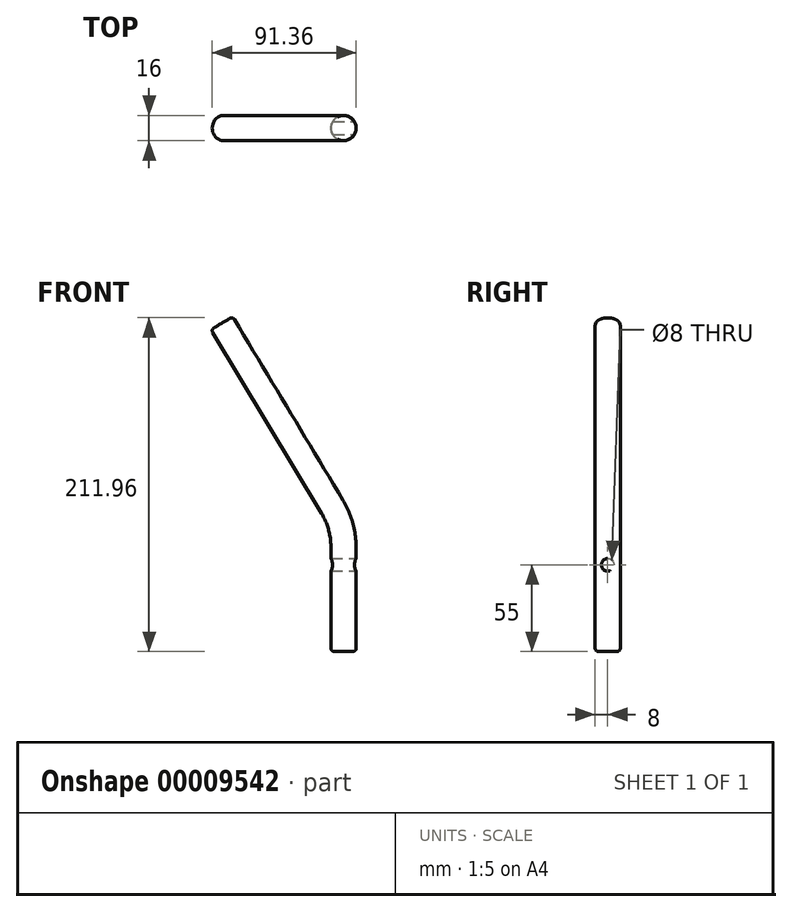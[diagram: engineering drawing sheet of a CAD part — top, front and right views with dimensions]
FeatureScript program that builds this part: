
annotation { "Feature Type Name" : "Feature", "Feature Type Description" : "" }
export const myFeature = defineFeature(function(context is Context, id is Id, definition is map)
    precondition{}
    {
        {
            var Q0;
            Q0=qCreatedBy(makeId("Top.planeOp"),FACE);
            var sketch = newSketch(context, id + "F0", { "sketchPlane" : qUnion([Q0])});
            skCircle(sketch, "E0", {"center": v(0, 0) * mm, "radius": 8 * mm});
            skSolve(sketch);
        }
        {
            var Q0;
            Q0=qCreatedBy(makeId("Right.planeOp"),FACE);
            var sketch = newSketch(context, id + "F1", { "sketchPlane" : qUnion([Q0])});
            skCircle(sketch, "E1", {"center": v(0, 55) * mm, "radius": 4 * mm});
            skSolve(sketch);
        }
        {
            var Q0;
            Q0=qCreatedBy(makeId("Front.planeOp"),FACE);
            var sketch = newSketch(context, id + "F2", { "sketchPlane" : qUnion([Q0])});
            skLineSegment(sketch, "E2", {"start": v(0, 0) * mm, "end": v(0, 66.14) * mm});
            skLineSegment(sketch, "E3", {"start": v(-7.14, 91.88) * mm, "end": v(-77.25, 208.58) * mm});
            skPoint(sketch, "E4.visualSharp", {"position": v(0, 80) * mm});
            skArc(sketch, "E4.filletArc", {"start": v(0, 66.14) * mm, "mid": v(-1.82, 79.5) * mm, "end": v(-7.14, 91.88) * mm});
            skSolve(sketch);
        }
        {
            var Q0;
            Q0=makeQuery(id+"F0.imprint","IMPRINT",FACE,{"disambiguationData":[TD([[makeQuery(id+"F0.imprint","IMPRINT",EDGE,{"derivedFrom":sQuery(id+"F0.wireOp",EDGE,"E0")}),1.0]])]});
            var Q1;
            Q1=sQuery(id+"F0.wireOp",EDGE,"E0");
            var Q2;
            Q2=sQuery(id+"F2.wireOp",EDGE,"E2");
            var Q3;
            Q3=sQuery(id+"F2.wireOp",EDGE,"E4.filletArc");
            var Q4;
            Q4=sQuery(id+"F2.wireOp",EDGE,"E3");
            sweep(context, id + "F3", {"profiles" : qUnion([Q0]), "surfaceProfiles" : qUnion([Q1]), "path" : qUnion([Q2, Q3, Q4])});
        }
        {
            var Q0;
            Q0 = qSketchRegion(id + "F1", true);
            extrude(context, id + "F4", {"entities" : qUnion([Q0]), "operationType" : NewBodyOperationType.REMOVE, "oppositeDirection" : true, "depth" : 25 * mm, "hasSecondDirection" : true, "secondDirectionOppositeDirection" : false, "secondDirectionDepth" : 25 * mm});
        }
        {
            var Q0;
            Q0=makeQuery(id+"F3.opSweep","CAP_EDGE",EDGE,{"disambiguationData":[OSD([sQuery(id+"F0.wireOp",EDGE,"E0"),sQuery(id+"F2.wireOp",VERTEX,"E2.start")])],"isStart":true});
            var Q1;
            Q1=makeQuery(id+"F3.opSweep","CAP_EDGE",EDGE,{"disambiguationData":[OSD([sQuery(id+"F0.wireOp",EDGE,"E0"),sQuery(id+"F2.wireOp",VERTEX,"E3.end")])],"isStart":false});
            fillet(context, id + "F5", {"entities" : qUnion([Q0, Q1]), "radius" : 2 * mm, "tangentPropagation" : true, "allowEdgeOverflow" : false});
        }
    });
